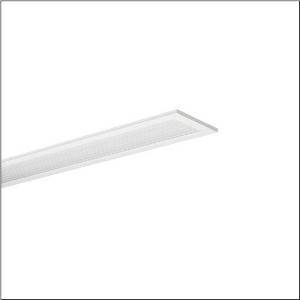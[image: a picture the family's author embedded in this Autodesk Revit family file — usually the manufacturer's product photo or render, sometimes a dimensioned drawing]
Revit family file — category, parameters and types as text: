
# Revit family: apollon_21_linear_51mq16wd2414
name_source: partatom
category: Lighting Fixtures
units: mm (PartAtom-declared; Revit-internal decimal feet)

## family parameters
Cut with Voids When Loaded = No
Host = Face
Light Source = No
Part Type = Normal
Room Calculation Point = No
Round Connector Dimension = Use Diameter
Shared = No

## types (1)
- Apollon 21 linear (1 x LED, 3400 lm, 23.2 W, 4000K)
    Apparent Load = 23 VA
    CIE Flux Codes = 64 88 97 100 100
    Color Rendering = 80
    Color Temperature = 4000K
    Default Elevation = 1800 mm
    Description = Apollon 21 linear, office luminaire, primary optical cover: micro prismatic cover, of PMMA, CAT 2 (L<= 3000cd/m²), light emission: direct distribution, primary light characteristic: symmetric, installation type: lay-in mounting, LED, rated luminous flux: 3.400lm, luminous efficacy: 147lm/W, light colour: 840, colour temperature: 4000K, control gear: DALI 2, Multilumen, with terminal, 5-pole, mains connection: 220..240V, AC/DC, 0/50..60Hz, rated input power: 23.2W, housing, of aluminium, coated, traffic white (RAL 9016), length: 1.545mm, width: 179mm, height: 55mm, recess depth: 180mm, housing upper side, of sheet steel, galvanised, protection rating (complete): IP20, protection rating (lamp compartment, on room side): IP50, insulation class (complete): insulation class II (safety insulation), certification: CE, ENEC, impact resistance: IK03, permissible operating ambient temperature: -20..+45°C, permissible storage temperature: -40..+80°C, standard: EN 60598-2-22, packaging unit: 1 piece
    Height = 0 mm  [stored 0 ft]
    Lamp = 1 x LED
    Lamp Light Flux = 3400 lm
    Lamp Power = 23.2 W
    Lamp count = 1
    Length = 1545 mm
    Luminous efficacy = 147 lm/W
    Manufacturer = Siteco
    ModVariant = No
    Model = 51MQ16WD2414
    Mounting Place = Ceiling
    Mounting Type = Recessed
    Number of Poles = 1
    OnlyDefault = Yes
    Power Factor = 1
    Product Name = Apollon 21 linear
    Product group = office luminaire | ceiling recessed
    ProductGroupID = 401
    Protection Class = Protection class II
    Protection Degree = IP 20
    RLX_Detail_Level = 1
    RLX_Emergency_Light_Flux = 0 lm
    RLX_Emergency_Type = 0
    RLX_Emergency_Type_DB = No
    RlxData = <blob elided: 12617 chars, md5=605f77d7>
    Socket = socket
    Standby Power = 0 W
    System Light Flux = 3400 lm
    System Power = 23 W
    Type Comments = Product without accessories
    Type Image = l_1291018.jpg
    URL = http://relux.com
    VarID = ---
    Voltage = 0 V
    Weight = 0.00 kg
    Width = 179 mm

note: [stored X ft] marks values corroborated as IEEE doubles in the binary element streams (Revit-internal decimal feet)

## geometry (parser evidence)
native form markers: Sweep x11
no freeform markers — native parametric forms only
